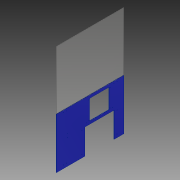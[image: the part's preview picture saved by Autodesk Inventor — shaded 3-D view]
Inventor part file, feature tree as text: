
AUTODESK INVENTOR PART (.ipt)
format: ipt  version: 2018 (Build 220112000, 112)  size: 219,136 bytes
history: native  units: in
note: dims shown in document units (in); Inventor stores cm internally (conversion verified against a paired STEP export)
features: plane x1, split x1, other x1
ambient origin geometry x8: Origin, YZ Plane, XZ Plane, XY Plane, X Axis, Y Axis, Z Axis, Center Point
bodies: Solid1 (feature_tree), Solid4 (feature_tree), Solid5 (feature_tree)
feature tree (3):
  plane  "Work Plane1"
  split  "Split4"
  other  "1_4 (0.25) Diameter Hole1"
